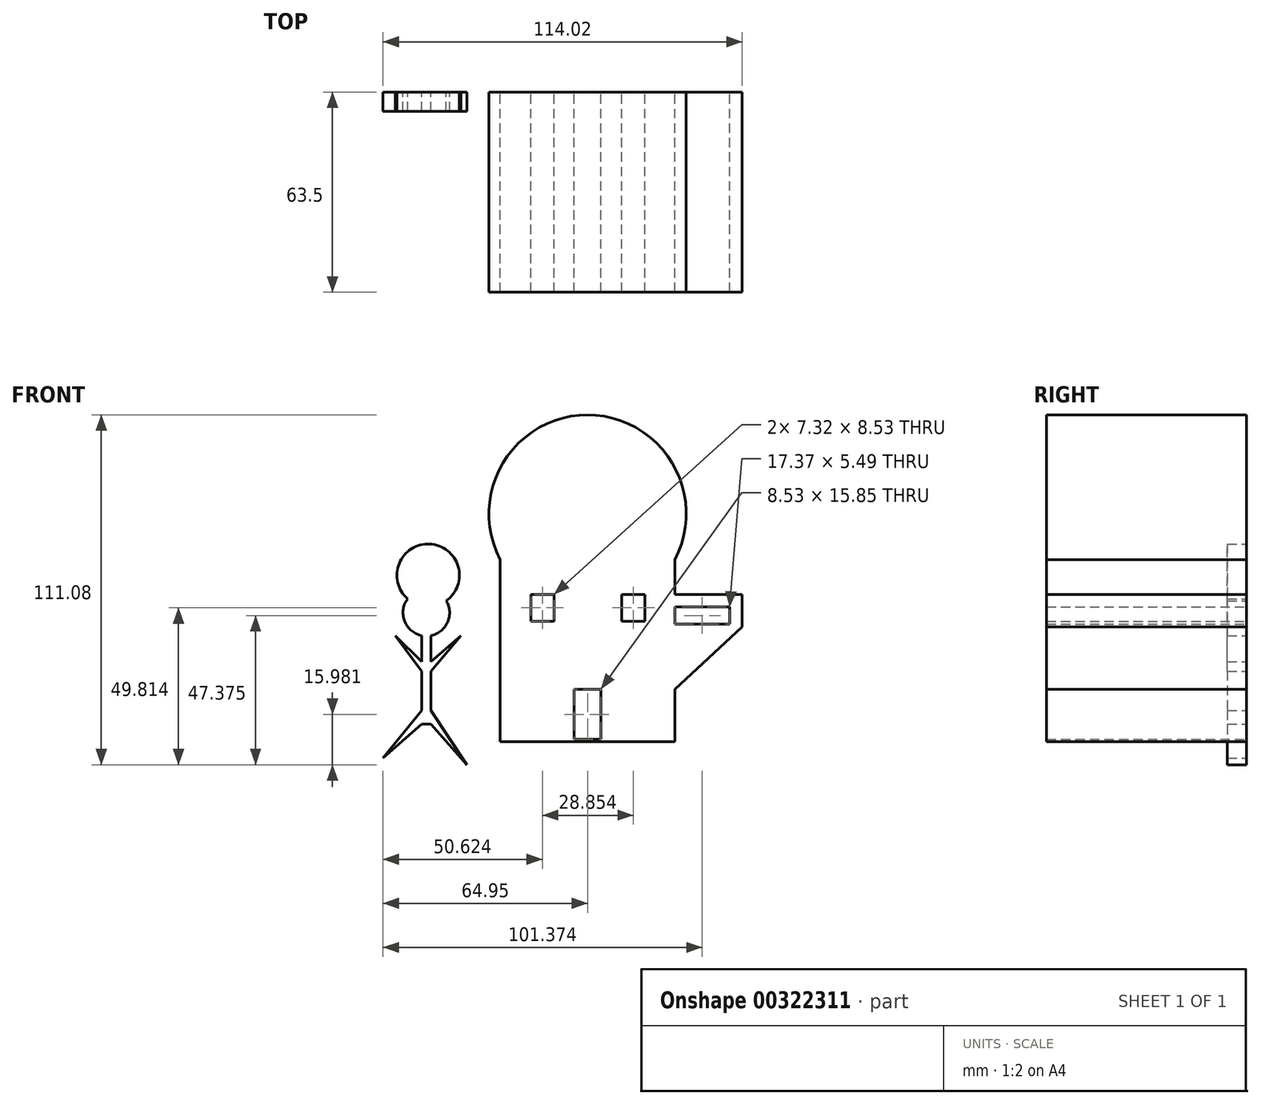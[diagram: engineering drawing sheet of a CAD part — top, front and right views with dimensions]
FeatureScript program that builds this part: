
annotation { "Feature Type Name" : "Feature", "Feature Type Description" : "" }
export const myFeature = defineFeature(function(context is Context, id is Id, definition is map)
    precondition{}
    {
        {
            var Q0;
            Q0=qCreatedBy(makeId("Front.planeOp"),FACE);
            var sketch = newSketch(context, id + "F0", { "sketchPlane" : qUnion([Q0])});
            skLineSegment(sketch, "E0.bottom", {"start": v(27.74, -28.92) * mm, "end": v(-27.74, -28.92) * mm});
            skLineSegment(sketch, "E0.top", {"start": v(27.74, 28.92) * mm, "end": v(-27.74, 28.92) * mm});
            skLineSegment(sketch, "E0.left", {"start": v(27.74, -28.92) * mm, "end": v(27.74, 28.92) * mm});
            skLineSegment(sketch, "E0.right", {"start": v(-27.74, -28.92) * mm, "end": v(-27.74, 28.92) * mm});
            skPoint(sketch, "E0.middle", {"position": v(0, 0) * mm});
            skArc(sketch, "E1", {"start": v(27.74, 28.92) * mm, "mid": v(0, 74.83) * mm, "end": v(-27.74, 28.92) * mm});
            skLineSegment(sketch, "E2.bottom", {"start": v(-17.98, 17.83) * mm, "end": v(-10.67, 17.83) * mm});
            skLineSegment(sketch, "E2.top", {"start": v(-17.98, 9.3) * mm, "end": v(-10.67, 9.3) * mm});
            skLineSegment(sketch, "E2.left", {"start": v(-17.98, 17.83) * mm, "end": v(-17.98, 9.3) * mm});
            skLineSegment(sketch, "E2.right", {"start": v(-10.67, 17.83) * mm, "end": v(-10.67, 9.3) * mm});
            skLineSegment(sketch, "E3.bottom", {"start": v(10.87, 17.83) * mm, "end": v(18.19, 17.83) * mm});
            skLineSegment(sketch, "E3.top", {"start": v(10.87, 9.3) * mm, "end": v(18.19, 9.3) * mm});
            skLineSegment(sketch, "E3.left", {"start": v(10.87, 17.83) * mm, "end": v(10.87, 9.3) * mm});
            skLineSegment(sketch, "E3.right", {"start": v(18.19, 17.83) * mm, "end": v(18.19, 9.3) * mm});
            skLineSegment(sketch, "E4", {"start": v(27.74, 8.38) * mm, "end": v(49.07, 8.38) * mm});
            skLineSegment(sketch, "E5", {"start": v(49.07, 7.47) * mm, "end": v(49.07, 17.83) * mm});
            skLineSegment(sketch, "E6", {"start": v(49.07, 17.83) * mm, "end": v(27.74, 17.83) * mm});
            skLineSegment(sketch, "E7", {"start": v(27.74, 13.87) * mm, "end": v(49.07, 13.87) * mm});
            skLineSegment(sketch, "E8", {"start": v(45.11, 13.87) * mm, "end": v(45.11, 8.38) * mm});
            skLineSegment(sketch, "E9", {"start": v(38.4, 13.87) * mm, "end": v(38.4, 8.38) * mm});
            skLineSegment(sketch, "E10", {"start": v(31.7, 13.87) * mm, "end": v(31.7, 8.38) * mm});
            skLineSegment(sketch, "E11", {"start": v(27.74, -12.34) * mm, "end": v(49.07, 7.47) * mm});
            skLineSegment(sketch, "E12.bottom", {"start": v(4.27, -12.34) * mm, "end": v(-4.27, -12.34) * mm});
            skLineSegment(sketch, "E12.top", {"start": v(4.27, -28.2) * mm, "end": v(-4.27, -28.2) * mm});
            skLineSegment(sketch, "E12.left", {"start": v(4.27, -12.34) * mm, "end": v(4.27, -28.2) * mm});
            skLineSegment(sketch, "E12.right", {"start": v(-4.27, -12.34) * mm, "end": v(-4.27, -28.2) * mm});
            skPoint(sketch, "E12.middle", {"position": v(0, -20.27) * mm});
            skSolve(sketch);
        }
        {
            var Q0;
            Q0 = qSketchRegion(id + "F0", true);
            extrude(context, id + "F1", {"entities" : qUnion([Q0]), "depth" : 63.5 * mm});
        }
        {
            var Q0;
            Q0=qCreatedBy(makeId("Front.planeOp"),FACE);
            var sketch = newSketch(context, id + "F2", { "sketchPlane" : qUnion([Q0])});
            skCircle(sketch, "E13", {"center": v(-51.2, 12.04) * mm, "radius": 7.4 * mm});
            skLineSegment(sketch, "E14.bottom", {"start": v(-52.66, 4.79) * mm, "end": v(-49.68, 4.79) * mm});
            skLineSegment(sketch, "E14.top", {"start": v(-52.66, -23.32) * mm, "end": v(-49.68, -23.32) * mm});
            skLineSegment(sketch, "E14.left", {"start": v(-52.66, 4.79) * mm, "end": v(-52.66, -23.32) * mm});
            skLineSegment(sketch, "E14.right", {"start": v(-49.68, 4.79) * mm, "end": v(-49.68, -23.32) * mm});
            skLineSegment(sketch, "E15", {"start": v(-49.68, -3.5) * mm, "end": v(-40.23, 4.79) * mm});
            skLineSegment(sketch, "E16", {"start": v(-52.66, -3.5) * mm, "end": v(-61, 4.79) * mm});
            skLineSegment(sketch, "E17", {"start": v(-49.68, -23.32) * mm, "end": v(-38.34, -36.25) * mm});
            skLineSegment(sketch, "E18", {"start": v(-52.66, -23.32) * mm, "end": v(-64.95, -34.1) * mm});
            skArc(sketch, "E19", {"start": v(-44.86, 15.84) * mm, "mid": v(-50.12, 33.84) * mm, "end": v(-57.14, 16.46) * mm});
            skLineSegment(sketch, "E20", {"start": v(-59.6, 19.73) * mm, "end": v(-41.17, 26.97) * mm});
            skLineSegment(sketch, "E21", {"start": v(-60.53, 23.93) * mm, "end": v(-43.29, 30.62) * mm});
            skLineSegment(sketch, "E22", {"start": v(-59.61, 28.1) * mm, "end": v(-46.78, 33.08) * mm});
            skLineSegment(sketch, "E23", {"start": v(-49.24, 19.17) * mm, "end": v(-41.17, 22.34) * mm});
            skLineSegment(sketch, "E24", {"start": v(-49.68, -6.55) * mm, "end": v(-40.23, 4.79) * mm});
            skLineSegment(sketch, "E25", {"start": v(-52.66, -6.55) * mm, "end": v(-61, 4.79) * mm});
            skLineSegment(sketch, "E26", {"start": v(-52.66, -19.05) * mm, "end": v(-64.95, -34.1) * mm});
            skLineSegment(sketch, "E27", {"start": v(-49.68, -19.05) * mm, "end": v(-38.34, -36.25) * mm});
            skLineSegment(sketch, "E28", {"start": v(-57.14, 16.46) * mm, "end": v(-44.86, 15.84) * mm});
            skSolve(sketch);
        }
        {
            var Q0;
            Q0 = qSketchRegion(id + "F2", true);
            extrude(context, id + "F3", {"entities" : qUnion([Q0]), "depth" : 6.1 * mm});
        }
    });
